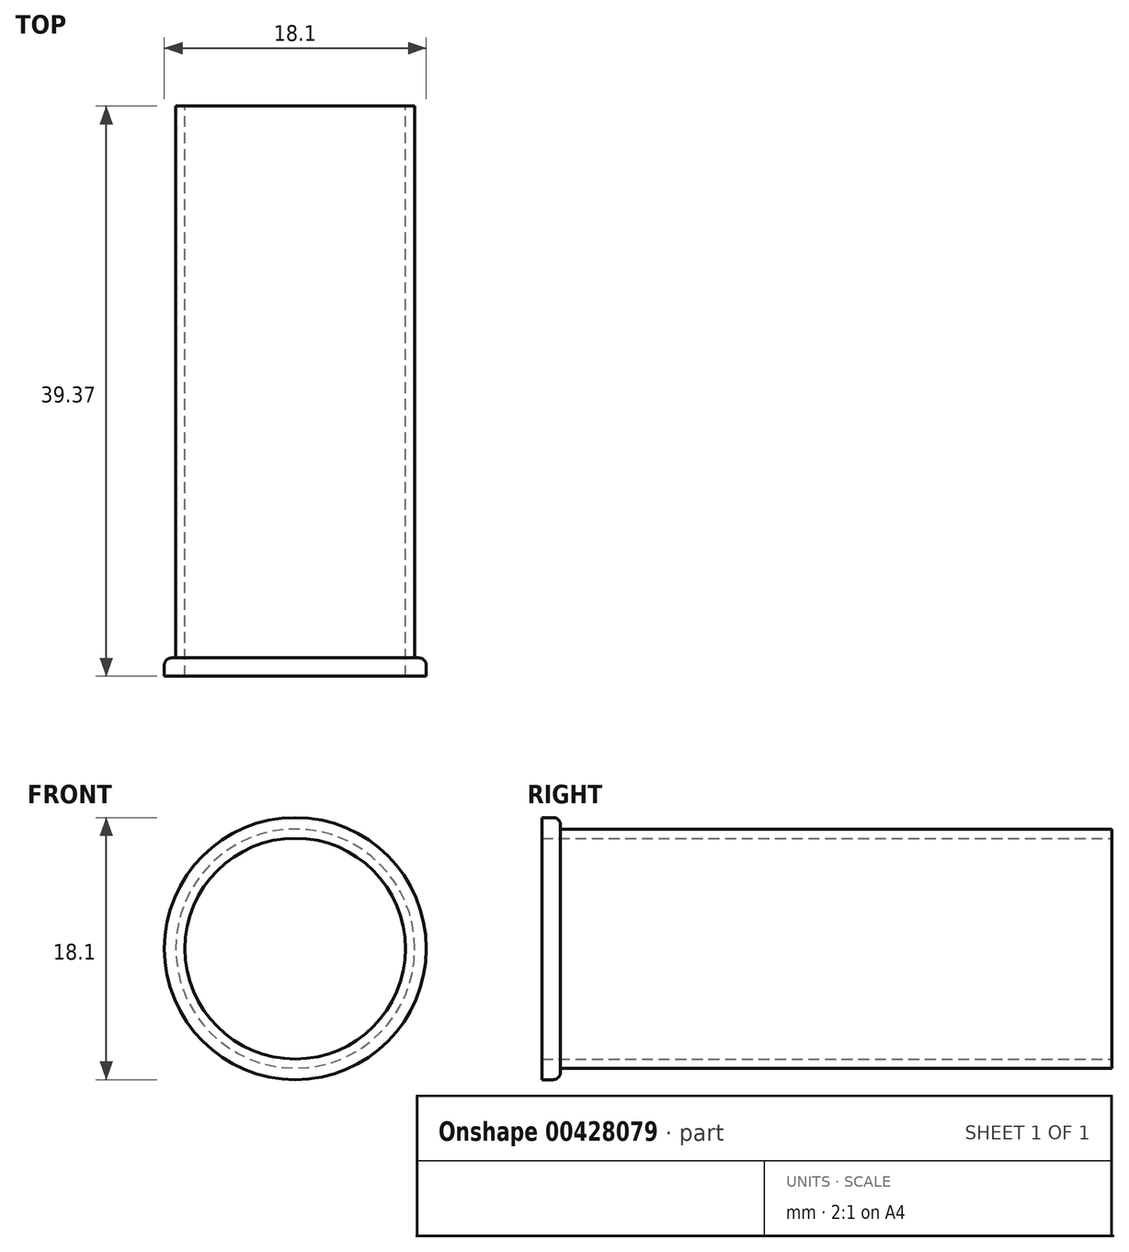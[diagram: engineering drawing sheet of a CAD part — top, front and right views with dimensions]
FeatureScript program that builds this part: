
annotation { "Feature Type Name" : "Feature", "Feature Type Description" : "" }
export const myFeature = defineFeature(function(context is Context, id is Id, definition is map)
    precondition{}
    {
        {
            var Q0;
            Q0=qCreatedBy(makeId("Front.planeOp"),FACE);
            var sketch = newSketch(context, id + "F0", { "sketchPlane" : qUnion([Q0])});
            skCircle(sketch, "E0", {"center": v(0, 0) * mm, "radius": 7.62 * mm});
            skCircle(sketch, "E1", {"center": v(0, 0) * mm, "radius": 8.26 * mm});
            skSolve(sketch);
        }
        {
            var Q0;
            Q0=makeQuery(id+"F0.imprint","IMPRINT",FACE,{"disambiguationData":[TD([[makeQuery(id+"F0.imprint","IMPRINT",EDGE,{"derivedFrom":sQuery(id+"F0.wireOp",EDGE,"E0")}),-1.0]])]});
            extrude(context, id + "F1", {"entities" : qUnion([Q0]), "depth" : 38.1 * mm});
        }
        {
            var Q0;
            Q0=makeQuery(id+"F1.opExtrude","CAP_FACE",FACE,{"disambiguationData":[OSD([sQuery(id+"F0.wireOp",EDGE,"E0"),sQuery(id+"F0.wireOp",EDGE,"E1")])],"isStart":false});
            var sketch = newSketch(context, id + "F2", { "sketchPlane" : qUnion([Q0])});
            skPoint(sketch, "E2.0", {"position": v(0, 0) * mm});
            skCircle(sketch, "E3", {"center": v(0, 0) * mm, "radius": 9.05 * mm});
            skCircle(sketch, "E4.0", {"center": v(0, 0) * mm, "radius": 8.26 * mm});
            skSolve(sketch);
        }
        {
            var Q0;
            Q0=makeQuery(id+"F2.imprint","IMPRINT",FACE,{"disambiguationData":[TD([[makeQuery(id+"F2.imprint","IMPRINT",EDGE,{"derivedFrom":sQuery(id+"F2.wireOp",EDGE,"E3")}),1.0]])]});
            var Q1;
            Q1=makeQuery(id+"F2.imprint","IMPRINT",FACE,{"disambiguationData":[TD([[makeQuery(id+"F2.imprint","IMPRINT",EDGE,{"derivedFrom":makeQuery(id+"F1.opExtrude","CAP_EDGE",EDGE,{"disambiguationData":[OSD([sQuery(id+"F0.wireOp",EDGE,"E0")])],"isStart":false})}),-1.0]])]});
            extrude(context, id + "F3", {"entities" : qUnion([Q0, Q1]), "operationType" : NewBodyOperationType.ADD, "depth" : 1.27 * mm});
        }
        {
            var Q0;
            Q0=makeQuery(id+"F3.opExtrude","CAP_EDGE",EDGE,{"disambiguationData":[OSD([sQuery(id+"F2.wireOp",EDGE,"E3")])],"isStart":true});
            fillet(context, id + "F4", {"entities" : qUnion([Q0]), "radius" : 0.5 * mm, "tangentPropagation" : true, "allowEdgeOverflow" : false});
        }
    });
